# Revit family: FP-Revit20-en-RB36S25MKIWN1-Cooldrawer-0-9000XXXXA-US-CA
name_source: partatom
category: Specialty Equipment
units: mm (PartAtom-declared; Revit-internal decimal feet)

## family parameters
Always vertical = Yes
Cut with Voids When Loaded = Yes
Part Type = Normal
Room Calculation Point = No
Round Connector Dimension = Use Diameter
Shared = No
Work Plane-Based = No

## types (4) — shared parameters
Cavity - Depth = 560.0 mm
Cavity - Height = 644.0 mm
Cavity - Width = 864.0 mm
Chassis - Depth = 557.0 mm
Chassis - Height = 640.0 mm
Chassis - Width = 855.0 mm
Connector Description - Electrical = 110 V, 60 Hz, 186 W
Default Elevation = 0.0 mm
Description = 36" Series 9 Integrated Cooldrawer™
Drawer Panel - Width = 896.0 mm
Manufacturer = Fisher&Paykel
Material - Body = Fisher & Paykel - Grey
Material - Structure = Fisher & Paykel - White
Model = RB36S25MKIWN1
Product - Depth = 557.0 mm
Product - Height = 640.0 mm
Product - Width = 855.0 mm
URL = www.fisherpaykel.com
Visibility - Clearance Required = Yes
Visibility - F&P Contemporary round handle = No
Visibility - F&P contemporary square fine black handle = No
Visibility - F&P contemporary square fine handle = No
Visibility - F&P stainless door panel kit 840545 = No

## per-type parameters (varying)
| type | Material - Trim | Visibility - Custom drawer panel (dual) | Visibility - Custom drawer panel (single) | Visibility - F&P contemporary square handle |
| RB36S25MKIWN1 with custom drawer panel (dual) | Fisher & Paykel - Stainless Steel | Yes | No | Yes |
| RB36S25MKIWN1 with custom drawer panel (single) | Fisher & Paykel - Stainless Steel | No | Yes | No |
| RB36S25MKIWN1 | Fisher & Paykel - White | No | No | No |
| RB36S25MKIWN1 with F&P door panel kit | Fisher & Paykel - Stainless Steel | Yes | No | Yes |

## geometry (parser evidence)
native form markers: Sweep x11
no freeform markers — native parametric forms only
